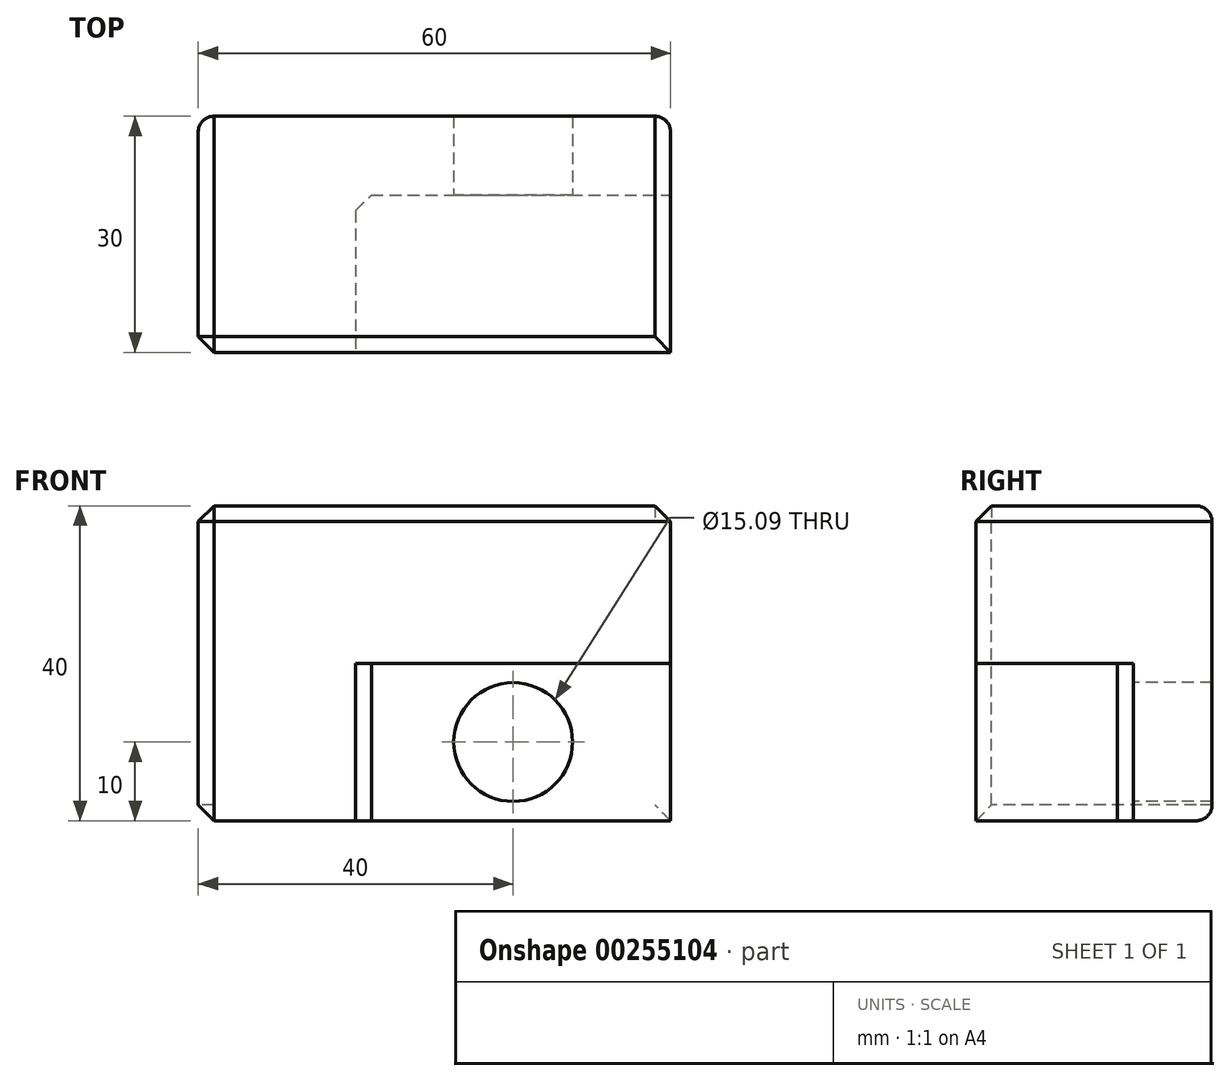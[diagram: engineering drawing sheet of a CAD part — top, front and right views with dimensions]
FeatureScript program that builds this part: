
annotation { "Feature Type Name" : "Feature", "Feature Type Description" : "" }
export const myFeature = defineFeature(function(context is Context, id is Id, definition is map)
    precondition{}
    {
        {
            var Q0;
            Q0=qCreatedBy(makeId("Front.planeOp"),FACE);
            var sketch = newSketch(context, id + "F0", { "sketchPlane" : qUnion([Q0])});
            skLineSegment(sketch, "E0.bottom", {"start": v(0, 0) * mm, "end": v(60, 0) * mm});
            skLineSegment(sketch, "E0.top", {"start": v(0, -40) * mm, "end": v(60, -40) * mm});
            skLineSegment(sketch, "E0.left", {"start": v(0, 0) * mm, "end": v(0, -40) * mm});
            skLineSegment(sketch, "E0.right", {"start": v(60, 0) * mm, "end": v(60, -40) * mm});
            skSolve(sketch);
        }
        {
            var Q0;
            Q0 = qSketchRegion(id + "F0", true);
            var Q1;
            Q1=makeQuery(id+"F0.imprint","IMPRINT",FACE,{"disambiguationData":[TD([[makeQuery(id+"F0.imprint","IMPRINT",EDGE,{"derivedFrom":sQuery(id+"F0.wireOp",EDGE,"E0.bottom")}),-1.0]])]});
            extrude(context, id + "F1", {"entities" : qUnion([Q0, Q1]), "depth" : 30 * mm});
        }
        {
            var Q0;
            Q0=makeQuery(id+"F1.opExtrude","CAP_FACE",FACE,{"disambiguationData":[OSD([sQuery(id+"F0.wireOp",EDGE,"E0.bottom"),sQuery(id+"F0.wireOp",EDGE,"E0.top"),sQuery(id+"F0.wireOp",EDGE,"E0.left"),sQuery(id+"F0.wireOp",EDGE,"E0.right")])],"isStart":false});
            var sketch = newSketch(context, id + "F2", { "sketchPlane" : qUnion([Q0])});
            skLineSegment(sketch, "E1.bottom", {"start": v(60, -40) * mm, "end": v(20, -40) * mm});
            skLineSegment(sketch, "E1.top", {"start": v(60, -20) * mm, "end": v(20, -20) * mm});
            skLineSegment(sketch, "E1.left", {"start": v(60, -40) * mm, "end": v(60, -20) * mm});
            skLineSegment(sketch, "E1.right", {"start": v(20, -40) * mm, "end": v(20, -20) * mm});
            skSolve(sketch);
        }
        {
            var Q0;
            Q0=makeQuery(id+"F2.imprint","IMPRINT",FACE,{"disambiguationData":[TD([[makeQuery(id+"F2.imprint","IMPRINT",EDGE,{"derivedFrom":sQuery(id+"F2.wireOp",EDGE,"E1.bottom")}),1.0]])]});
            extrude(context, id + "F3", {"entities" : qUnion([Q0]), "operationType" : NewBodyOperationType.REMOVE, "oppositeDirection" : true, "depth" : 20 * mm});
        }
        {
            var Q0;
            Q0=makeQuery(id+"F3.boolean.opBoolean","COPY",FACE,{"derivedFrom":makeQuery(id+"F3.opExtrude","CAP_FACE",FACE,{"disambiguationData":[OSD([sQuery(id+"F2.wireOp",EDGE,"E1.bottom"),sQuery(id+"F2.wireOp",EDGE,"E1.top"),sQuery(id+"F2.wireOp",EDGE,"E1.left"),sQuery(id+"F2.wireOp",EDGE,"E1.right")])],"isStart":false})});
            var sketch = newSketch(context, id + "F4", { "sketchPlane" : qUnion([Q0])});
            skCircle(sketch, "E2", {"center": v(40, -30) * mm, "radius": 7.54 * mm});
            skSolve(sketch);
        }
        {
            var Q0;
            Q0=makeQuery(id+"F4.imprint","IMPRINT",FACE,{"disambiguationData":[TD([[makeQuery(id+"F4.imprint","IMPRINT",EDGE,{"derivedFrom":sQuery(id+"F4.wireOp",EDGE,"E2")}),1.0]])]});
            extrude(context, id + "F5", {"entities" : qUnion([Q0]), "operationType" : NewBodyOperationType.REMOVE, "endBound" : BoundingType.THROUGH_ALL, "oppositeDirection" : true, "depth" : 25 * mm});
        }
        {
            var Q0;
            Q0=makeQuery(id+"F1.opExtrude","CAP_EDGE",EDGE,{"disambiguationData":[OSD([sQuery(id+"F0.wireOp",EDGE,"E0.bottom")])],"isStart":true});
            var Q1;
            Q1=makeQuery(id+"F1.opExtrude","CAP_EDGE",EDGE,{"disambiguationData":[OSD([sQuery(id+"F0.wireOp",EDGE,"E0.right")])],"isStart":true});
            var Q2;
            Q2=makeQuery(id+"F1.opExtrude","CAP_EDGE",EDGE,{"disambiguationData":[OSD([sQuery(id+"F0.wireOp",EDGE,"E0.top")])],"isStart":true});
            var Q3;
            Q3=makeQuery(id+"F1.opExtrude","CAP_EDGE",EDGE,{"disambiguationData":[OSD([sQuery(id+"F0.wireOp",EDGE,"E0.left")])],"isStart":true});
            fillet(context, id + "F6", {"entities" : qUnion([Q0, Q1, Q2, Q3]), "radius" : 2 * mm, "tangentPropagation" : true, "allowEdgeOverflow" : false});
        }
        {
            var Q0;
            Q0=makeQuery(id+"F3.boolean.opBoolean","COPY",EDGE,{"derivedFrom":makeQuery(id+"F3.opExtrude","CAP_EDGE",EDGE,{"disambiguationData":[OSD([sQuery(id+"F2.wireOp",EDGE,"E1.top")])],"isStart":true})});
            var Q1;
            Q1=makeQuery(id+"F3.boolean.opBoolean","COPY",EDGE,{"derivedFrom":makeQuery(id+"F3.opExtrude","SWEPT_EDGE",EDGE,{"disambiguationData":[OSD([sQuery(id+"F0.wireOp",EDGE,"E0.right"),sQuery(id+"F2.wireOp",EDGE,"E1.top"),sQuery(id+"F2.wireOp",EDGE,"E1.left")])]})});
            var Q2;
            Q2=makeQuery(id+"F3.boolean.opBoolean","COPY",EDGE,{"derivedFrom":makeQuery(id+"F3.opExtrude","CAP_EDGE",EDGE,{"disambiguationData":[OSD([sQuery(id+"F2.wireOp",EDGE,"E1.right")])],"isStart":true})});
            var Q3;
            Q3=makeQuery(id+"F3.boolean.opBoolean","COPY",EDGE,{"derivedFrom":makeQuery(id+"F3.opExtrude","CAP_EDGE",EDGE,{"disambiguationData":[OSD([sQuery(id+"F2.wireOp",EDGE,"E1.right")])],"isStart":false})});
            var Q4;
            Q4=makeQuery(id+"F1.opExtrude","CAP_EDGE",EDGE,{"disambiguationData":[OSD([sQuery(id+"F0.wireOp",EDGE,"E0.left")])],"isStart":false});
            var Q5;
            Q5=makeQuery(id+"F1.opExtrude","SWEPT_EDGE",EDGE,{"disambiguationData":[OSD([sQuery(id+"F0.wireOp",EDGE,"E0.bottom"),sQuery(id+"F0.wireOp",EDGE,"E0.right")])]});
            var Q6;
            Q6=makeQuery(id+"F1.opExtrude","SWEPT_EDGE",EDGE,{"disambiguationData":[OSD([sQuery(id+"F0.wireOp",EDGE,"E0.top"),sQuery(id+"F0.wireOp",EDGE,"E0.left")])]});
            var Q7;
            Q7=makeQuery(id+"F3.boolean.opBoolean","COPY",EDGE,{"derivedFrom":makeQuery(id+"F3.opExtrude","CAP_EDGE",EDGE,{"disambiguationData":[OSD([sQuery(id+"F2.wireOp",EDGE,"E1.bottom")])],"isStart":false})});
            var Q8;
            Q8=makeQuery(id+"F3.boolean.opBoolean","COPY",EDGE,{"derivedFrom":makeQuery(id+"F3.opExtrude","CAP_EDGE",EDGE,{"disambiguationData":[OSD([sQuery(id+"F2.wireOp",EDGE,"E1.left")])],"isStart":false})});
            var Q9;
            Q9=makeQuery(id+"F1.opExtrude","CAP_EDGE",EDGE,{"disambiguationData":[OSD([sQuery(id+"F0.wireOp",EDGE,"E0.bottom")])],"isStart":false});
            var Q10;
            Q10=makeQuery(id+"F1.opExtrude","SWEPT_EDGE",EDGE,{"disambiguationData":[OSD([sQuery(id+"F0.wireOp",EDGE,"E0.bottom"),sQuery(id+"F0.wireOp",EDGE,"E0.left")])]});
            chamfer(context, id + "F7", {"entities" : qUnion([Q0, Q1, Q2, Q3, Q4, Q5, Q6, Q7, Q8, Q9, Q10]), "width" : 2 * mm, "tangentPropagation" : true});
        }
    });
